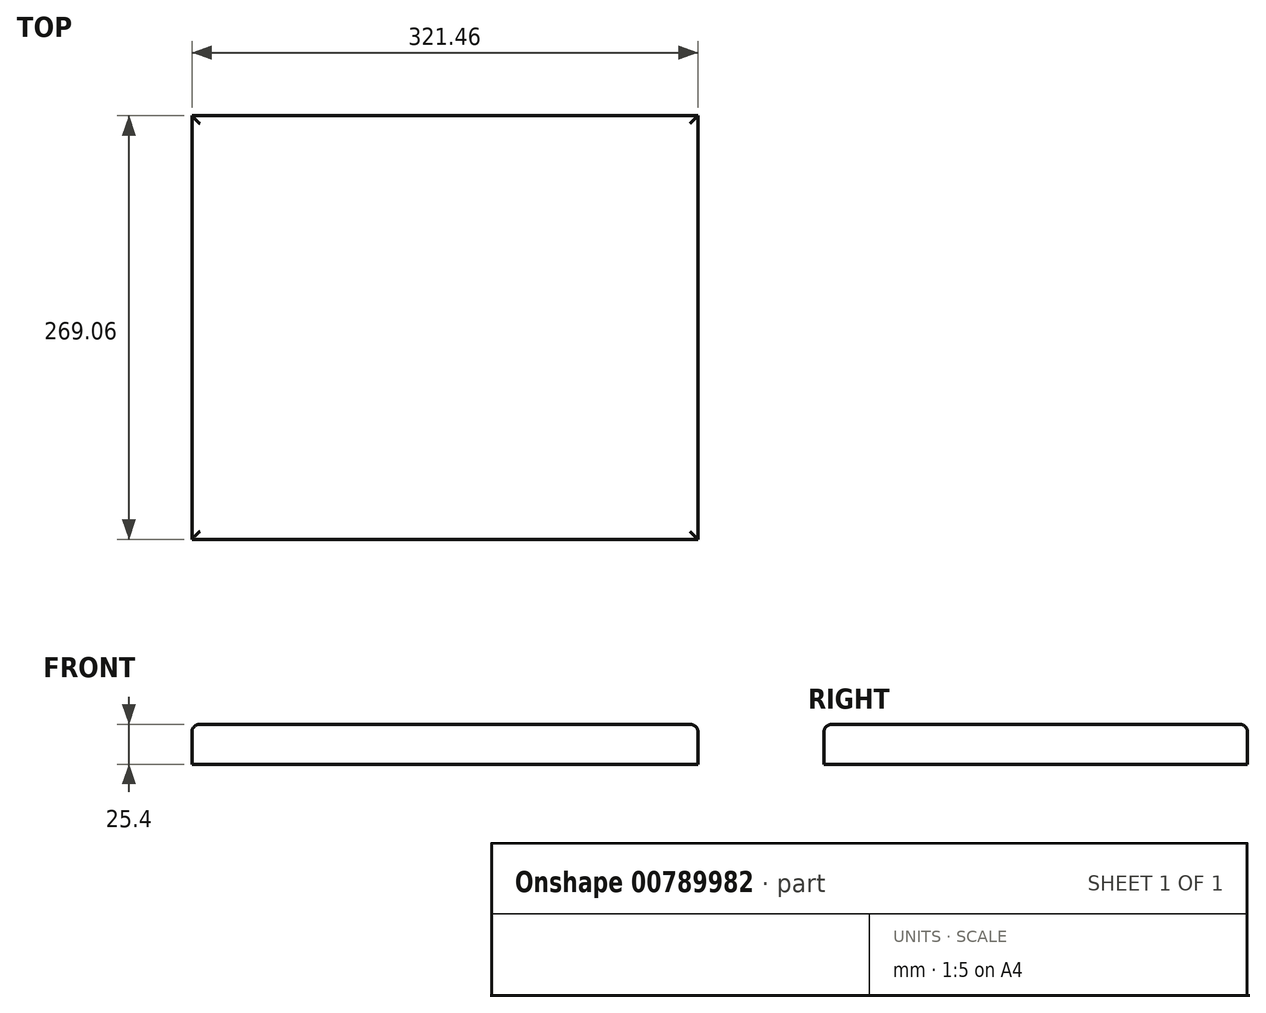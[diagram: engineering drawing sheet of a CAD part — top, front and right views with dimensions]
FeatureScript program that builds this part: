
annotation { "Feature Type Name" : "Feature", "Feature Type Description" : "" }
export const myFeature = defineFeature(function(context is Context, id is Id, definition is map)
    precondition{}
    {
        {
            var Q0;
            Q0=qCreatedBy(makeId("Top.planeOp"),FACE);
            var sketch = newSketch(context, id + "F0", { "sketchPlane" : qUnion([Q0])});
            skLineSegment(sketch, "E0.bottom", {"start": v(-160.73, -134.53) * mm, "end": v(160.73, -134.53) * mm});
            skLineSegment(sketch, "E0.top", {"start": v(-160.73, 134.53) * mm, "end": v(160.73, 134.53) * mm});
            skLineSegment(sketch, "E0.left", {"start": v(-160.73, -134.53) * mm, "end": v(-160.73, 134.53) * mm});
            skLineSegment(sketch, "E0.right", {"start": v(160.73, -134.53) * mm, "end": v(160.73, 134.53) * mm});
            skPoint(sketch, "E0.middle", {"position": v(0, 0) * mm});
            skSolve(sketch);
        }
        {
            var Q0;
            Q0=makeQuery(id+"F0.imprint","IMPRINT",FACE,{"disambiguationData":[TD([[makeQuery(id+"F0.imprint","IMPRINT",EDGE,{"derivedFrom":sQuery(id+"F0.wireOp",EDGE,"E0.bottom")}),1.0]])]});
            extrude(context, id + "F1", {"entities" : qUnion([Q0]), "depth" : 25.4 * mm, "offsetDistance" : 25.4 * mm});
        }
        {
            var Q0;
            Q0=makeQuery(id+"F1.opExtrude","CAP_FACE",FACE,{"disambiguationData":[OSD([sQuery(id+"F0.wireOp",EDGE,"E0.bottom"),sQuery(id+"F0.wireOp",EDGE,"E0.top"),sQuery(id+"F0.wireOp",EDGE,"E0.left"),sQuery(id+"F0.wireOp",EDGE,"E0.right")])],"isStart":false});
            fillet(context, id + "F2", {"entities" : qUnion([Q0]), "radius" : 5.08 * mm, "tangentPropagation" : true, "allowEdgeOverflow" : false});
        }
        {
            var Q0;
            Q0=qCreatedBy(makeId("Top.planeOp"),FACE);
            cPlane(context, id + "F3", {"entities" : qUnion([Q0]), "cplaneType" : CPlaneType.OFFSET, "offset" : 33.78 * mm, "width" : 152.4 * mm, "height" : 152.4 * mm});
        }
    });
